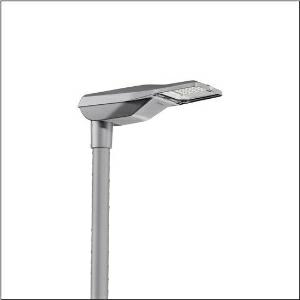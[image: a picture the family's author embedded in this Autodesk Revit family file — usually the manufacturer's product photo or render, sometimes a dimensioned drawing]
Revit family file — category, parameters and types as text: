
# Revit family: streetlight_sl_21_iq_micro___st0_8a_5xe1c41d08cb_e31f
name_source: partatom
category: Lighting Fixtures
units: mm (PartAtom-declared; Revit-internal decimal feet)

## family parameters
Cut with Voids When Loaded = No
Host = Face
Light Source = No
Part Type = Normal
Room Calculation Point = No
Round Connector Dimension = Use Diameter
Shared = No

## types (1)
- --- (1 x LED, 2980 lm, 19.4 W, 4000K)
    Apparent Load = 19 VA
    CIE Flux Codes = 38 75 97 100 100
    Color Rendering = 70
    Color Temperature = 4000K
    Default Elevation = 1800 mm
    Description = Streetlight SL 21 iQ micro, mast luminaire, primary light control with lens, of PMMA, primary optical cover: cover, of toughened safety glass, transparent, light distribution: ST0.8a, light emission: direct distribution, primary light characteristic: asymmetric, installation type: post-top, side-entry, LED, High Power LED, rated luminous flux: 2.980lm, luminous efficacy: 154lm/W, light colour: 740, colour temperature: 4000K, control gear: iQ-Comfort, control: Auto-Match, Temp-Guard, Lumen-Switch, Night-Set, Smart-Wire, Light-Fading, Desk-Remote (wireless, voltage-free reading and setting of iQ features in the workshop via application-optimized NFC function/RFID function), optimised constant luminous flux control (CLO 2.0), pre-setting: linear dimming characteristic, mains connection: 220..240V, AC, 50/60Hz, start of lifetime: 19W, end of service life: 20W, reduction: 10W, luminaire housing, of diecast aluminium, powder-coated, Siteco® metallic grey (DB 702S), corrosivity category C5 mid according to DIN EN ISO 12944, please order mast flange separately, inclination adjustable: 0°, 5°, 10°, 15°, sealing non-destructively replaceable, multi-level sealing system, length: 528mm, width: 235mm, height: 110mm, mast flange for spigot size: 42mm (side-entry): 5XC10008XM4, 60/48mm (side-entry/post-top): 5XC10108XM2, 76/60mm (side-entry/post-top): 5XC10108XM1, protection rating (complete): IP66, insulation class (complete): insulation class II (safety insulation), certification: CE, ENEC, ENEC+, VDE, impact resistance: IK10, permissible operating ambient temperature for outdoor applications: -40..+50°C, standard-compliant lighting for roads and squares, packaging unit: 1 piece

Light Distribution: ST0.8a
    Height = 110 mm
    Lamp = 1 x LED
    Lamp Light Flux = 2980 lm
    Lamp Power = 19.4 W
    Lamp count = 1
    Length = 528 mm
    Luminous efficacy = 154 lm/W
    Manufacturer = Siteco
    ModVariant = No
    Model = 5XE1C41D08CB
    Number of Poles = 1
    OnlyDefault = Yes
    Power Factor = 1
    Product Name = Streetlight SL 21 iQ micro | ST0.8a
    Product group = mast luminaire | pylon top
    ProductGroupID = 6100
    Protection Class = Protection class II
    Protection Degree = IP 66
    RLX_Detail_Level = 1
    RLX_Emergency_Light_Flux = 0 lm
    RLX_Emergency_Type = 0
    RLX_Emergency_Type_DB = No
    RlxData = <blob elided: 98973 chars, md5=4fd7d4c3>
    Socket = socket
    Standby Power = 0 W
    System Light Flux = 2980 lm
    System Power = 19 W
    Type Comments = factory setting: luminous flux: 100 % | dim-lin: 254 | 387 mA
    Type Image = l_1006881.jpg
    URL = http://relux.com
    VarID = @adj_138392
    Voltage = 0 V
    Weight = 0.00 kg
    Width = 235 mm

## geometry (parser evidence)
native form markers: Blend x4, Sweep x9
no freeform markers — native parametric forms only
